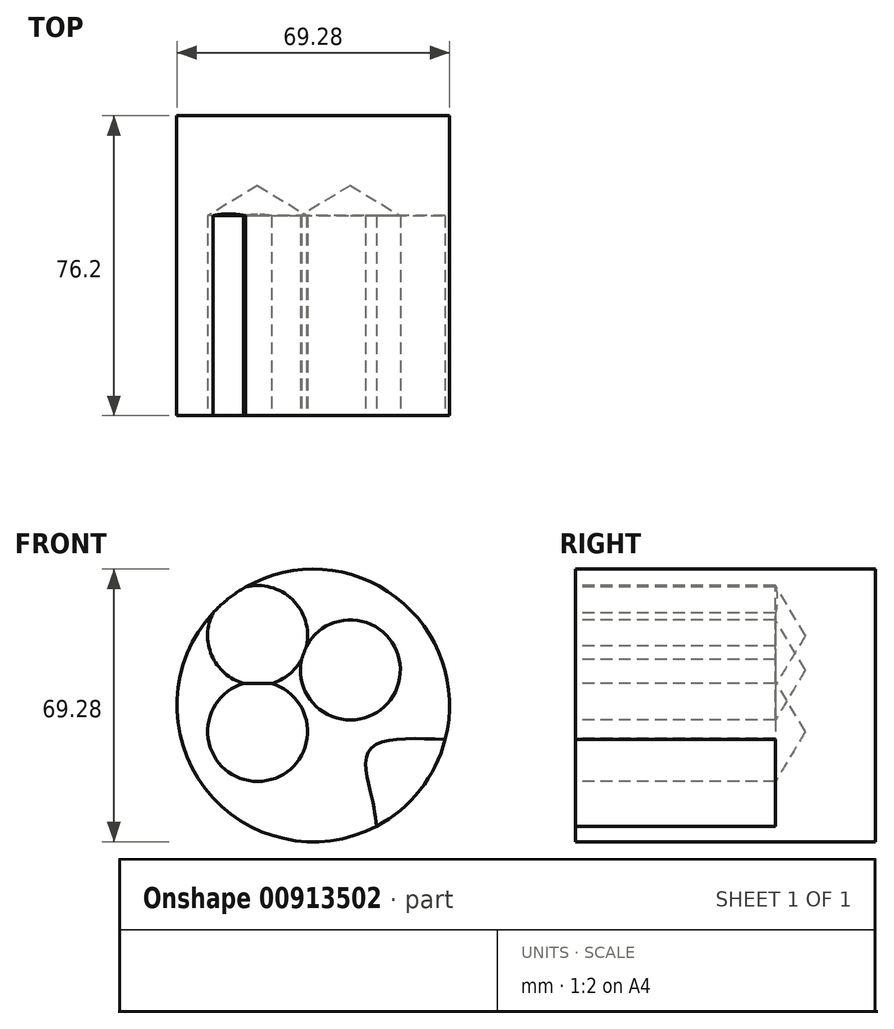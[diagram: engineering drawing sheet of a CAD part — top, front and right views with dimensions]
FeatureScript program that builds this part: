
annotation { "Feature Type Name" : "Feature", "Feature Type Description" : "" }
export const myFeature = defineFeature(function(context is Context, id is Id, definition is map)
    precondition{}
    {
        {
            var Q0;
            Q0=qCreatedBy(makeId("Front.planeOp"),FACE);
            var sketch = newSketch(context, id + "F0", { "sketchPlane" : qUnion([Q0])});
            skCircle(sketch, "E0", {"center": v(0, 0) * mm, "radius": 34.64 * mm});
            skSolve(sketch);
        }
        {
            var Q0;
            Q0 = qSketchRegion(id + "F0", true);
            extrude(context, id + "F1", {"entities" : qUnion([Q0]), "depth" : 76.2 * mm, "offsetDistance" : 25.4 * mm});
        }
        {
            var Q0;
            Q0=makeQuery(id+"F1.opExtrude","CAP_FACE",FACE,{"disambiguationData":[OSD([sQuery(id+"F0.wireOp",EDGE,"E0")])],"isStart":false});
            var sketch = newSketch(context, id + "F2", { "sketchPlane" : qUnion([Q0])});
            skPoint(sketch, "E1", {"position": v(95.78, 85.35) * mm});
            skPoint(sketch, "E2", {"position": v(100.22, 65.73) * mm});
            skPoint(sketch, "E3", {"position": v(119.64, 85.35) * mm});
            skPoint(sketch, "E4", {"position": v(-14.1, -6.6) * mm});
            skPoint(sketch, "E5", {"position": v(-14.1, 17.78) * mm});
            skPoint(sketch, "E6", {"position": v(9.45, 9.03) * mm});
            skPoint(sketch, "E7", {"position": v(-321.2, -59.76) * mm});
            skFitSpline(sketch, "E8", {"points": [v(33.54, -8.68) * mm, v(14.26, -11.4) * mm, v(14.82, -23.14) * mm, v(16.12, -30.67) * mm], "startDerivative": vector(-60.39, 3.02) * mm, "endDerivative": vector(3.23, -25.48) * mm});
            skFitSpline(sketch, "E9", {"points": [v(33.54, -8.68) * mm, v(52.89, -23.1) * mm, v(39.1, -44.5) * mm, v(16.12, -30.67) * mm], "startDerivative": vector(84.52, -32.41) * mm, "endDerivative": vector(-67.2, 70.03) * mm});
            skSolve(sketch);
        }
        {
            var Q0;
            Q0=sQuery(id+"F2.wireOp",VERTEX,"E4");
            var Q1;
            Q1=sQuery(id+"F2.wireOp",VERTEX,"E5");
            var Q2;
            Q2=sQuery(id+"F2.wireOp",VERTEX,"E6");
            var Q3;
            Q3=makeQuery(id+"F1.opExtrude","SWEPT_BODY",BODY,{"disambiguationData":[OSD([sQuery(id+"F0.wireOp",EDGE,"E0")])]});
            hole(context, id + "F3", {"style" : HoleStyle.SIMPLE, "endStyle" : HoleEndStyle.BLIND, "holeDiameter" : 25.4 * mm, "majorDiameter" : 6.35 * mm, "holeDepth" : 50.8 * mm, "isTappedThrough" : true, "tappedDepth" : 12.7 * mm, "tapClearance" : 3, "locations" : qUnion([Q0, Q1, Q2]), "scope" : qUnion([Q3])});
        }
        {
            var Q0;
            Q0 = qSketchRegion(id + "F2", true);
            extrude(context, id + "F4", {"entities" : qUnion([Q0]), "operationType" : NewBodyOperationType.REMOVE, "oppositeDirection" : true, "depth" : 50.8 * mm, "offsetDistance" : 25.4 * mm});
        }
    });
